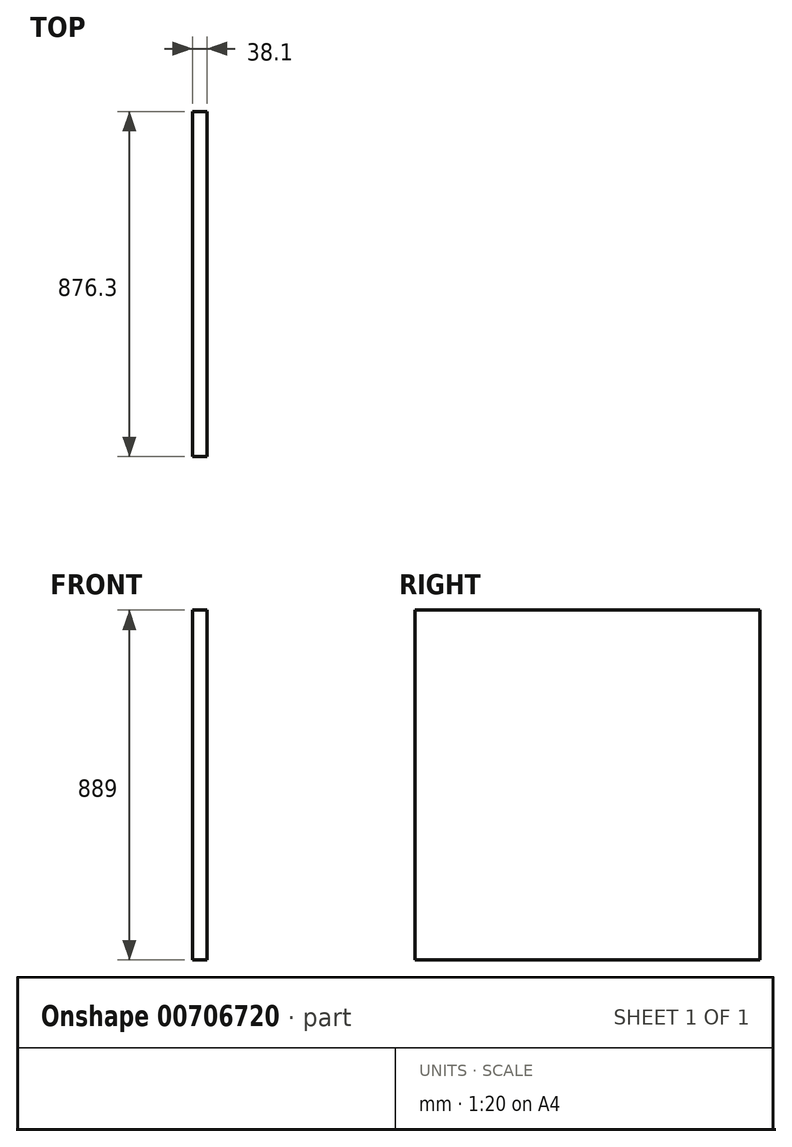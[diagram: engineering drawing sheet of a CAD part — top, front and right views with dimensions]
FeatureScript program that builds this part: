
annotation { "Feature Type Name" : "Feature", "Feature Type Description" : "" }
export const myFeature = defineFeature(function(context is Context, id is Id, definition is map)
    precondition{}
    {
        {
            var Q0;
            Q0=qCreatedBy(makeId("Right.planeOp"),FACE);
            var sketch = newSketch(context, id + "F0", { "sketchPlane" : qUnion([Q0])});
            skLineSegment(sketch, "E0.bottom", {"start": v(0, 0) * mm, "end": v(876.3, 0) * mm});
            skLineSegment(sketch, "E0.top", {"start": v(0, 889) * mm, "end": v(876.3, 889) * mm});
            skLineSegment(sketch, "E0.left", {"start": v(0, 0) * mm, "end": v(0, 889) * mm});
            skLineSegment(sketch, "E0.right", {"start": v(876.3, 0) * mm, "end": v(876.3, 889) * mm});
            skSolve(sketch);
        }
        {
            var Q0;
            Q0=makeQuery(id+"F0.imprint","IMPRINT",FACE,{"disambiguationData":[TD([[makeQuery(id+"F0.imprint","IMPRINT",EDGE,{"derivedFrom":sQuery(id+"F0.wireOp",EDGE,"E0.bottom")}),1.0]])]});
            extrude(context, id + "F1", {"entities" : qUnion([Q0]), "depth" : 38.1 * mm, "offsetDistance" : 25.4 * mm});
        }
    });
